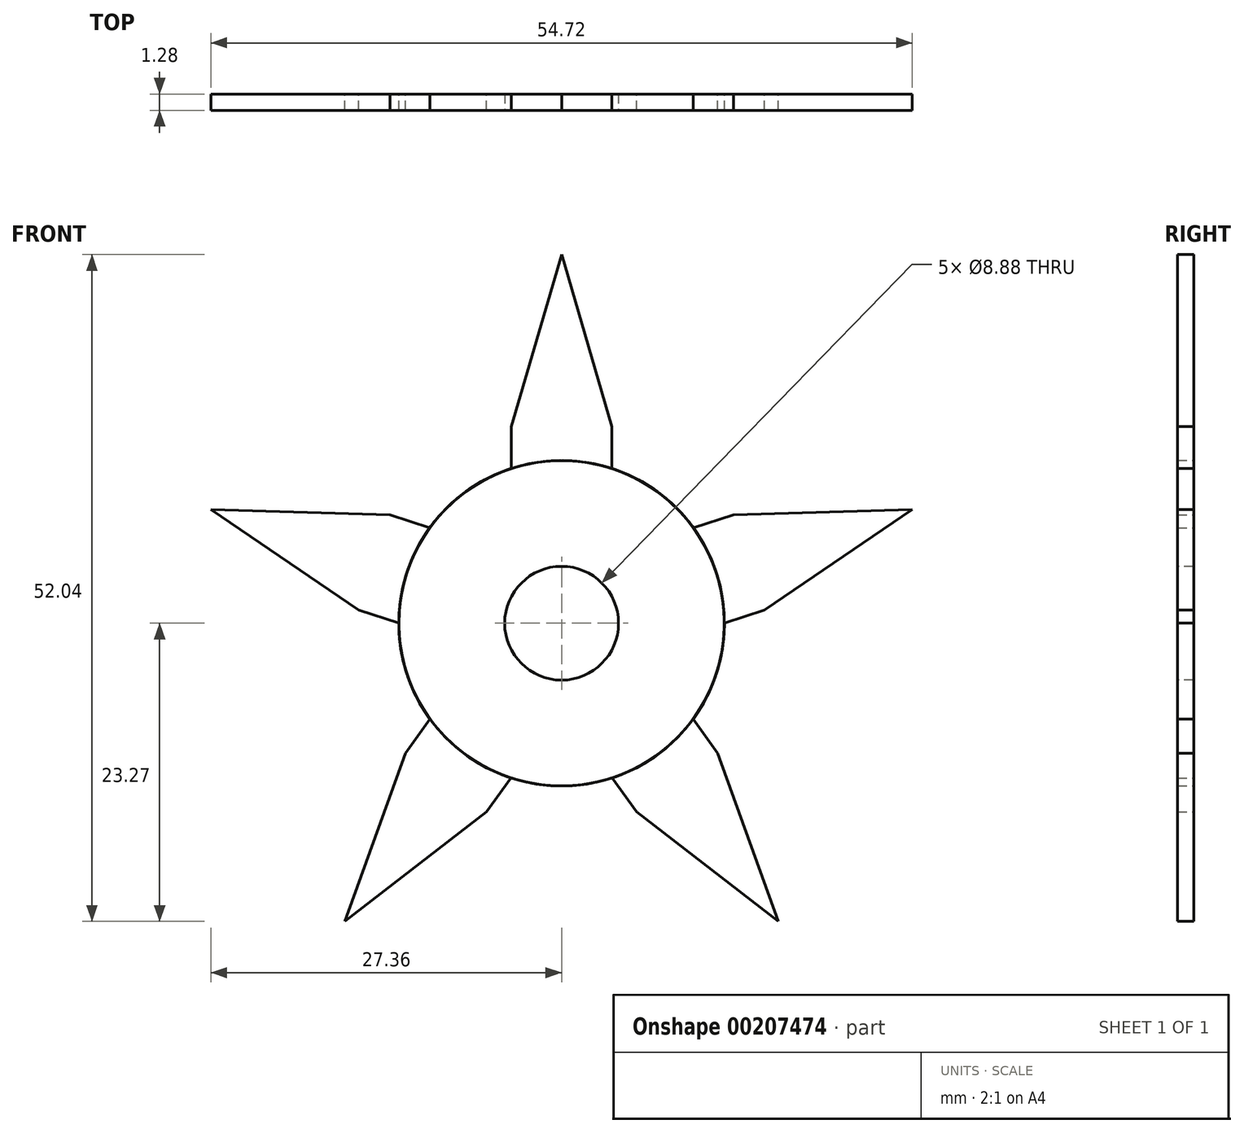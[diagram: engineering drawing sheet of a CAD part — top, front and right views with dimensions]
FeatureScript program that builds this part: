
annotation { "Feature Type Name" : "Feature", "Feature Type Description" : "" }
export const myFeature = defineFeature(function(context is Context, id is Id, definition is map)
    precondition{}
    {
        {
            var Q0;
            Q0=qCreatedBy(makeId("Front.planeOp"),FACE);
            var sketch = newSketch(context, id + "F0", { "sketchPlane" : qUnion([Q0])});
            skCircle(sketch, "E0", {"center": v(0, 0) * mm, "radius": 12.7 * mm});
            skSolve(sketch);
        }
        {
            var Q0;
            Q0=qSketchRegion(id+"F0",true);
            extrude(context, id + "F1", {"entities" : qUnion([Q0]), "endBound" : BoundingType.SYMMETRIC, "depth" : 1.27 * mm});
        }
        {
            var Q0;
            Q0=qCreatedBy(makeId("Front.planeOp"),FACE);
            var sketch = newSketch(context, id + "F2", { "sketchPlane" : qUnion([Q0])});
            skLineSegment(sketch, "E1.bottom", {"start": v(3.9, 15.36) * mm, "end": v(-3.9, 15.36) * mm});
            skLineSegment(sketch, "E1.top", {"start": v(3.9, 9.4) * mm, "end": v(-3.9, 9.4) * mm});
            skLineSegment(sketch, "E1.left", {"start": v(3.9, 15.36) * mm, "end": v(3.9, 9.4) * mm});
            skLineSegment(sketch, "E1.right", {"start": v(-3.9, 15.36) * mm, "end": v(-3.9, 9.4) * mm});
            skPoint(sketch, "E1.middle", {"position": v(0, 12.38) * mm});
            skLineSegment(sketch, "E2", {"start": v(-3.9, 15.36) * mm, "end": v(0, 28.77) * mm});
            skLineSegment(sketch, "E3", {"start": v(0, 28.77) * mm, "end": v(3.9, 15.36) * mm});
            skSolve(sketch);
        }
        {
            var Q0;
            Q0=qSketchRegion(id+"F2",true);
            extrude(context, id + "F3", {"entities" : qUnion([Q0]), "operationType" : NewBodyOperationType.ADD, "endBound" : BoundingType.SYMMETRIC, "depth" : 1.27 * mm});
        }
        {
            var Q0;
            Q0=makeQuery(id+"F1.opExtrude","SWEPT_BODY",BODY,{"disambiguationData":[OSD([sQuery(id+"F0.wireOp",EDGE,"E0")])]});
            var Q1;
            Q1=sQuery(id+"F0.wireOp",EDGE,"E0");
            circularPattern(context, id + "F4", {"entities" : qUnion([Q0]), "axis" : qUnion([Q1]), "angle" : 360 * degree, "instanceCount" : 5, "equalSpace" : true});
        }
        {
            var Q0;
            Q0=qCreatedBy(makeId("Front.planeOp"),FACE);
            var sketch = newSketch(context, id + "F5", { "sketchPlane" : qUnion([Q0])});
            skCircle(sketch, "E4", {"center": v(0, 0) * mm, "radius": 4.44 * mm});
            skSolve(sketch);
        }
        {
            var Q0;
            Q0=qSketchRegion(id+"F5",true);
            extrude(context, id + "F6", {"entities" : qUnion([Q0]), "operationType" : NewBodyOperationType.REMOVE, "endBound" : BoundingType.SYMMETRIC, "oppositeDirection" : true, "depth" : 1.27 * mm});
        }
    });
